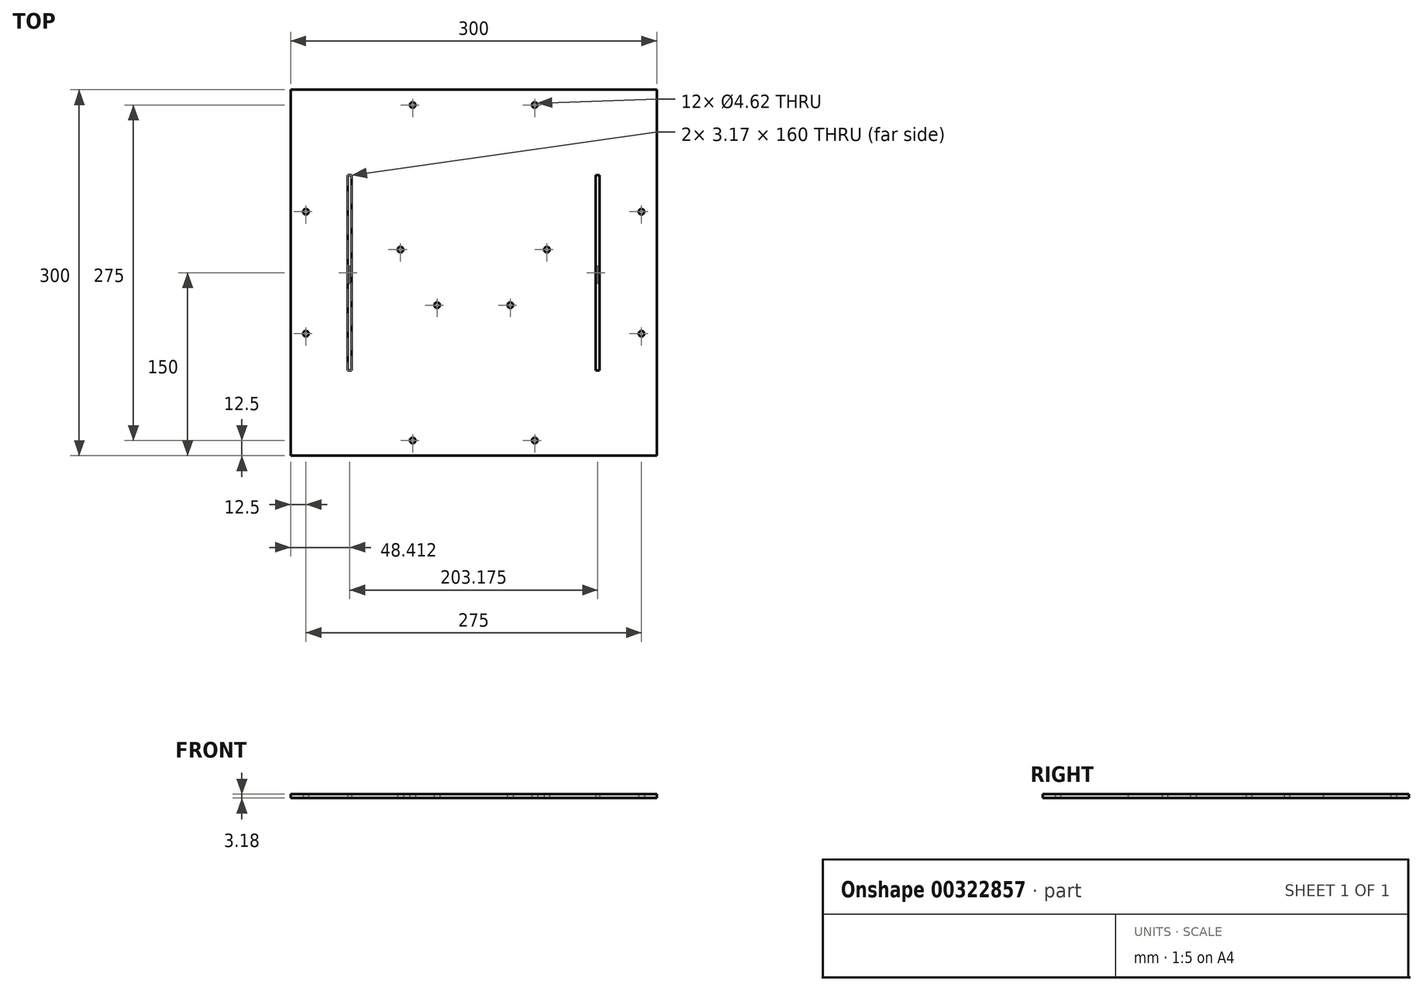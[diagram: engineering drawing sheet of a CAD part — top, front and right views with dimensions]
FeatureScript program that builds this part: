
annotation { "Feature Type Name" : "Feature", "Feature Type Description" : "" }
export const myFeature = defineFeature(function(context is Context, id is Id, definition is map)
    precondition{}
    {
        {
            var Q0;
            Q0=qCreatedBy(makeId("Top.planeOp"),FACE);
            var sketch = newSketch(context, id + "F0", { "sketchPlane" : qUnion([Q0])});
            skLineSegment(sketch, "E0.bottom", {"start": v(150, -150) * mm, "end": v(-150, -150) * mm});
            skLineSegment(sketch, "E0.top", {"start": v(150, 150) * mm, "end": v(-150, 150) * mm});
            skLineSegment(sketch, "E0.left", {"start": v(150, -150) * mm, "end": v(150, 150) * mm});
            skLineSegment(sketch, "E0.right", {"start": v(-150, -150) * mm, "end": v(-150, 150) * mm});
            skPoint(sketch, "E0.middle", {"position": v(0, 0) * mm});
            skLineSegment(sketch, "E1.left", {"start": v(100, -80) * mm, "end": v(100, 80) * mm});
            skLineSegment(sketch, "E1.right", {"start": v(-100, -80) * mm, "end": v(-100, 80) * mm});
            skLineSegment(sketch, "E2.bottom", {"start": v(103.17, -80) * mm, "end": v(100, -80) * mm});
            skLineSegment(sketch, "E2.top", {"start": v(103.17, 80) * mm, "end": v(100, 80) * mm});
            skLineSegment(sketch, "E2.left", {"start": v(103.17, -80) * mm, "end": v(103.17, 80) * mm});
            skLineSegment(sketch, "E2.right", {"start": v(-103.17, -80) * mm, "end": v(-103.17, 80) * mm});
            skLineSegment(sketch, "E3.bottom", {"start": v(50, 137.5) * mm, "end": v(47.69, 137.5) * mm});
            skLineSegment(sketch, "E3.top", {"start": v(50, 162.5) * mm, "end": v(-50, 162.5) * mm});
            skLineSegment(sketch, "E3.left", {"start": v(50, 137.5) * mm, "end": v(50, 139.81) * mm});
            skLineSegment(sketch, "E3.right", {"start": v(-50, 137.5) * mm, "end": v(-50, 139.81) * mm});
            skPoint(sketch, "E3.middle", {"position": v(0, 150) * mm});
            skCircle(sketch, "E4", {"center": v(50, 137.5) * mm, "radius": 2.31 * mm});
            skCircle(sketch, "E5", {"center": v(-50, 137.5) * mm, "radius": 2.31 * mm});
            skLineSegment(sketch, "E6.trimOffspring", {"start": v(-47.69, 137.5) * mm, "end": v(-50, 137.5) * mm});
            skLineSegment(sketch, "E7.trimOffspring", {"start": v(-50, 150) * mm, "end": v(-50, 162.5) * mm});
            skLineSegment(sketch, "E8.trimOffspring", {"start": v(50, 150) * mm, "end": v(50, 162.5) * mm});
            skLineSegment(sketch, "E9.trimOffspring", {"start": v(-100, 80) * mm, "end": v(-103.17, 80) * mm});
            skLineSegment(sketch, "E10.trimOffspring", {"start": v(-100, -80) * mm, "end": v(-103.18, -80) * mm});
            skLineSegment(sketch, "E11", {"start": v(0, 0) * mm, "end": v(25, 0) * mm});
            skLineSegment(sketch, "E12", {"start": v(25, 0) * mm, "end": v(0, 0) * mm});
            skLineSegment(sketch, "E13", {"start": v(0, 0) * mm, "end": v(0, -25) * mm});
            skCircle(sketch, "E14", {"center": v(-30, -26.57) * mm, "radius": 2.31 * mm});
            skCircle(sketch, "E15.MirrorC", {"center": v(30, -26.57) * mm, "radius": 2.31 * mm});
            skCircle(sketch, "E16", {"center": v(-60, 18.97) * mm, "radius": 2.31 * mm});
            skCircle(sketch, "E17", {"center": v(60, 18.97) * mm, "radius": 2.31 * mm});
            skLineSegment(sketch, "E18", {"start": v(0, -26.57) * mm, "end": v(0, -10.45) * mm});
            skLineSegment(sketch, "E19", {"start": v(0, 0) * mm, "end": v(0, -10.45) * mm});
            skCircle(sketch, "E20.1.0", {"center": v(-137.5, 50) * mm, "radius": 2.31 * mm});
            skCircle(sketch, "E20.1.1", {"center": v(-137.5, -50) * mm, "radius": 2.31 * mm});
            skCircle(sketch, "E20.2.0", {"center": v(-50, -137.5) * mm, "radius": 2.31 * mm});
            skCircle(sketch, "E20.2.1", {"center": v(50, -137.5) * mm, "radius": 2.31 * mm});
            skCircle(sketch, "E20.3.0", {"center": v(137.5, -50) * mm, "radius": 2.31 * mm});
            skCircle(sketch, "E20.3.1", {"center": v(137.5, 50) * mm, "radius": 2.31 * mm});
            skSolve(sketch);
        }
        {
            var Q0;
            Q0=makeQuery(id+"F0.imprint","IMPRINT",FACE,{"disambiguationData":[TD([[makeQuery(id+"F0.imprint","IMPRINT",EDGE,{"derivedFrom":sQuery(id+"F0.wireOp",EDGE,"E0.bottom")}),-1.0]])]});
            extrude(context, id + "F1", {"entities" : qUnion([Q0]), "depth" : 3.17 * mm});
        }
    });
